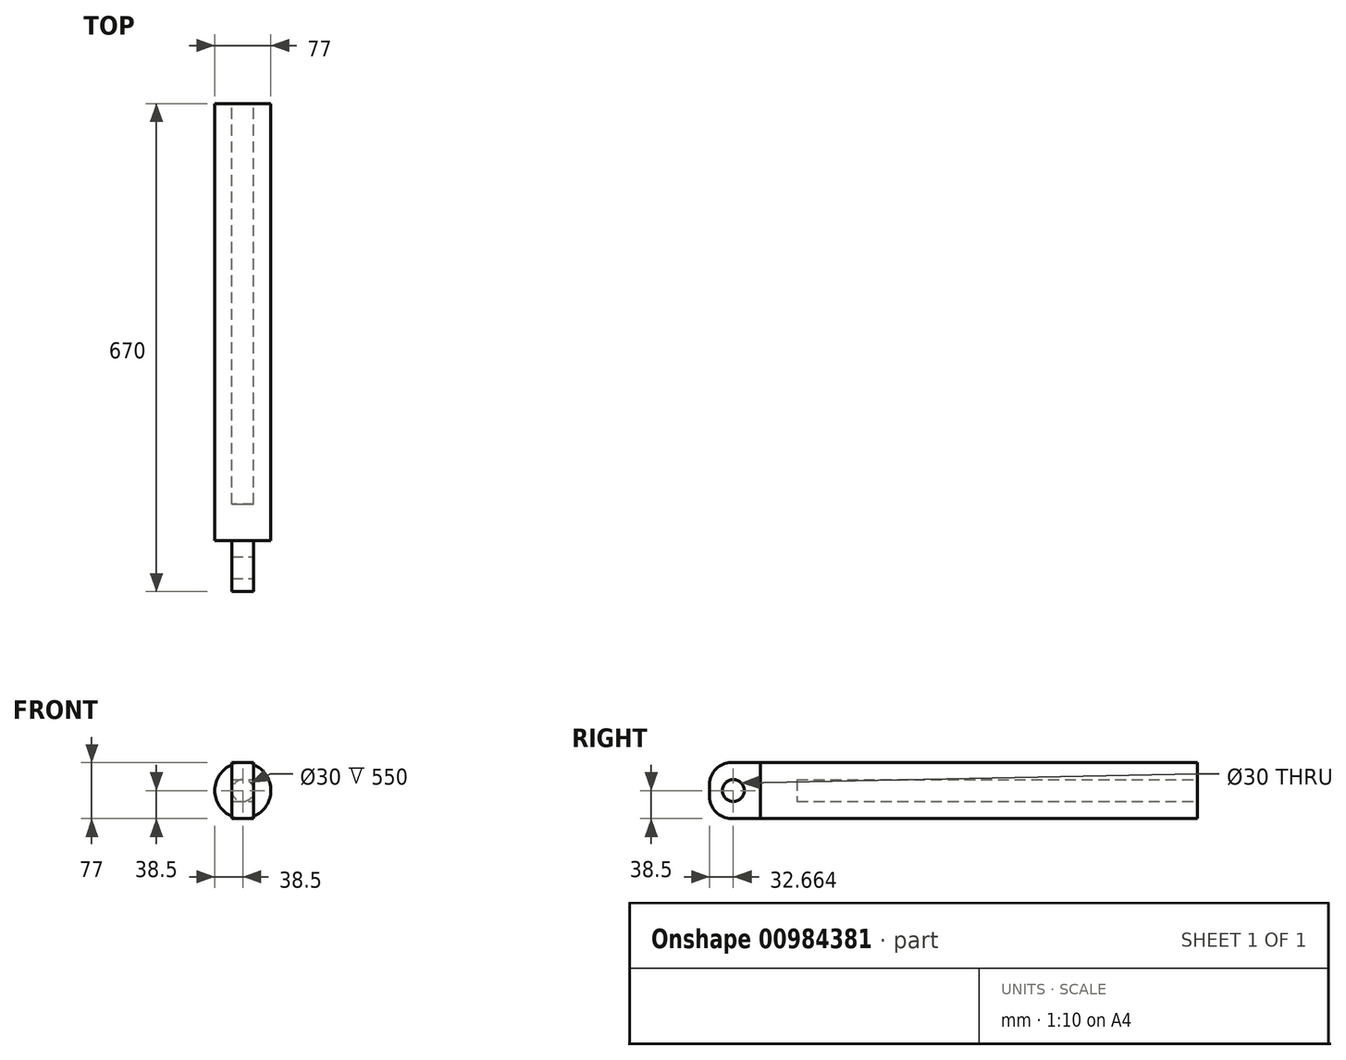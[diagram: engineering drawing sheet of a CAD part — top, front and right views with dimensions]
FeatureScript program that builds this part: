
annotation { "Feature Type Name" : "Feature", "Feature Type Description" : "" }
export const myFeature = defineFeature(function(context is Context, id is Id, definition is map)
    precondition{}
    {
        {
            var Q0;
            Q0=qCreatedBy(makeId("Front.planeOp"),FACE);
            var sketch = newSketch(context, id + "F0", { "sketchPlane" : qUnion([Q0])});
            skCircle(sketch, "E0", {"center": v(0, 0) * mm, "radius": 38.5 * mm});
            skSolve(sketch);
        }
        {
            var Q0;
            Q0=qSketchRegion(id+"F0",true);
            extrude(context, id + "F1", {"entities" : qUnion([Q0]), "oppositeDirection" : true, "depth" : 600 * mm, "offsetDistance" : 25 * mm});
        }
        {
            var Q0;
            Q0=makeQuery(id+"F1.opExtrude","CAP_FACE",FACE,{"disambiguationData":[OSD([sQuery(id+"F0.wireOp",EDGE,"E0")])],"isStart":true});
            var sketch = newSketch(context, id + "F2", { "sketchPlane" : qUnion([Q0])});
            skLineSegment(sketch, "E1.bottom", {"start": v(15, -38.5) * mm, "end": v(-15, -38.5) * mm});
            skLineSegment(sketch, "E1.top", {"start": v(15, 38.5) * mm, "end": v(-15, 38.5) * mm});
            skLineSegment(sketch, "E1.left", {"start": v(15, -38.5) * mm, "end": v(15, 38.5) * mm});
            skLineSegment(sketch, "E1.right", {"start": v(-15, -38.5) * mm, "end": v(-15, 38.5) * mm});
            skPoint(sketch, "E1.middle", {"position": v(0, 0) * mm});
            skSolve(sketch);
        }
        {
            var Q0;
            Q0=qSketchRegion(id+"F2",true);
            extrude(context, id + "F3", {"entities" : qUnion([Q0]), "operationType" : NewBodyOperationType.ADD, "depth" : 70 * mm, "offsetDistance" : 25 * mm});
        }
        {
            var Q0;
            Q0=makeQuery(id+"F3.opExtrude","SWEPT_FACE",FACE,{"disambiguationData":[OSD([sQuery(id+"F2.wireOp",EDGE,"E1.left")])]});
            var sketch = newSketch(context, id + "F4", { "sketchPlane" : qUnion([Q0])});
            skCircle(sketch, "E2", {"center": v(-37.34, 0) * mm, "radius": 15 * mm});
            skSolve(sketch);
        }
        {
            var Q0;
            Q0=makeQuery(id+"F4.imprint","IMPRINT",FACE,{"disambiguationData":[TD([[makeQuery(id+"F4.imprint","IMPRINT",EDGE,{"derivedFrom":sQuery(id+"F4.wireOp",EDGE,"E2")}),1.0]])]});
            extrude(context, id + "F5", {"entities" : qUnion([Q0]), "operationType" : NewBodyOperationType.REMOVE, "endBound" : BoundingType.THROUGH_ALL, "oppositeDirection" : true, "depth" : 25 * mm, "offsetDistance" : 25 * mm});
        }
        {
            var Q0;
            Q0=makeQuery(id+"F3.opExtrude","CAP_EDGE",EDGE,{"disambiguationData":[OSD([sQuery(id+"F2.wireOp",EDGE,"E1.top")])],"isStart":false});
            var Q1;
            Q1=makeQuery(id+"F3.opExtrude","CAP_EDGE",EDGE,{"disambiguationData":[OSD([sQuery(id+"F2.wireOp",EDGE,"E1.bottom")])],"isStart":false});
            fillet(context, id + "F6", {"entities" : qUnion([Q0, Q1]), "radius" : 30 * mm, "tangentPropagation" : true, "allowEdgeOverflow" : false});
        }
        {
            var Q0;
            Q0=makeQuery(id+"F1.opExtrude","CAP_FACE",FACE,{"disambiguationData":[OSD([sQuery(id+"F0.wireOp",EDGE,"E0")])],"isStart":false});
            var sketch = newSketch(context, id + "F7", { "sketchPlane" : qUnion([Q0])});
            skCircle(sketch, "E3", {"center": v(0, 0) * mm, "radius": 15 * mm});
            skSolve(sketch);
        }
        {
            var Q0;
            Q0=makeQuery(id+"F7.imprint","IMPRINT",FACE,{"disambiguationData":[TD([[makeQuery(id+"F7.imprint","IMPRINT",EDGE,{"derivedFrom":sQuery(id+"F7.wireOp",EDGE,"E3")}),1.0]])]});
            extrude(context, id + "F8", {"entities" : qUnion([Q0]), "operationType" : NewBodyOperationType.REMOVE, "oppositeDirection" : true, "depth" : 550 * mm, "offsetDistance" : 25 * mm});
        }
    });
